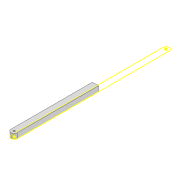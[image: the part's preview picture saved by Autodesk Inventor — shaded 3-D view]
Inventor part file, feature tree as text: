
AUTODESK INVENTOR PART (.ipt)
format: ipt  version: 2022 (Build 260153000, 153)  size: 116,224 bytes
history: native  units: mm
features: sketch x5, extrude x4, projected_geometry x2
ambient origin geometry x8: Origin, YZ Plane, XZ Plane, XY Plane, X Axis, Y Axis, Z Axis, Center Point
bodies: Solid1 (feature_tree)
feature tree (11):
  extrude  "Extrusion1"  Depth=10.0mm
  extrude  "Extrusion2"  Depth=3.0mm
  sketch  "Sketch3"  dims[d4=8.0mm d5=0.0mm d12=10.0mm]
  extrude  "Extrusion3"  Depth=10.0mm
  extrude  "Extrusion4"  Depth=20.0mm
  sketch  "Sketch1"  dims[d0=244.795mm d1=10.0mm]
  sketch  "Sketch2"  dims[d2=3.0mm d3=3.0mm]
  projected_geometry  "Projected Loop1"
  projected_geometry  "Projected Loop2"
  sketch  "Sketch4"  dims[d13=12.0mm d14=0.0mm d15=20.0mm]
  sketch  "Sketch5"  dims[d16=3.0mm d17=0.0mm d18=100.0mm d19=0.0mm]
